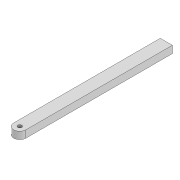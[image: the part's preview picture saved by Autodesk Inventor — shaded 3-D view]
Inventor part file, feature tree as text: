
AUTODESK INVENTOR PART (.ipt)
format: ipt  version: 2022 (Build 260153000, 153)  size: 95,744 bytes
history: native  units: mm
features: extrude x2, sketch x2
ambient origin geometry x8: Origin, YZ Plane, XZ Plane, XY Plane, X Axis, Y Axis, Z Axis, Center Point
bodies: Solid1 (feature_tree)
feature tree (4):
  extrude  "Extrusion1"  Depth=3.3mm
  extrude  "Extrusion2"  Depth=6.0mm
  sketch  "Sketch1"  dims[d0=3.3mm d1=3.3mm]
  sketch  "Sketch3"  dims[d2=10.0mm d3=261.6mm d4=3.3mm d5=153.559mm d6=6.0mm d7=0.0mm d8=100.0mm d9=0.0mm]
